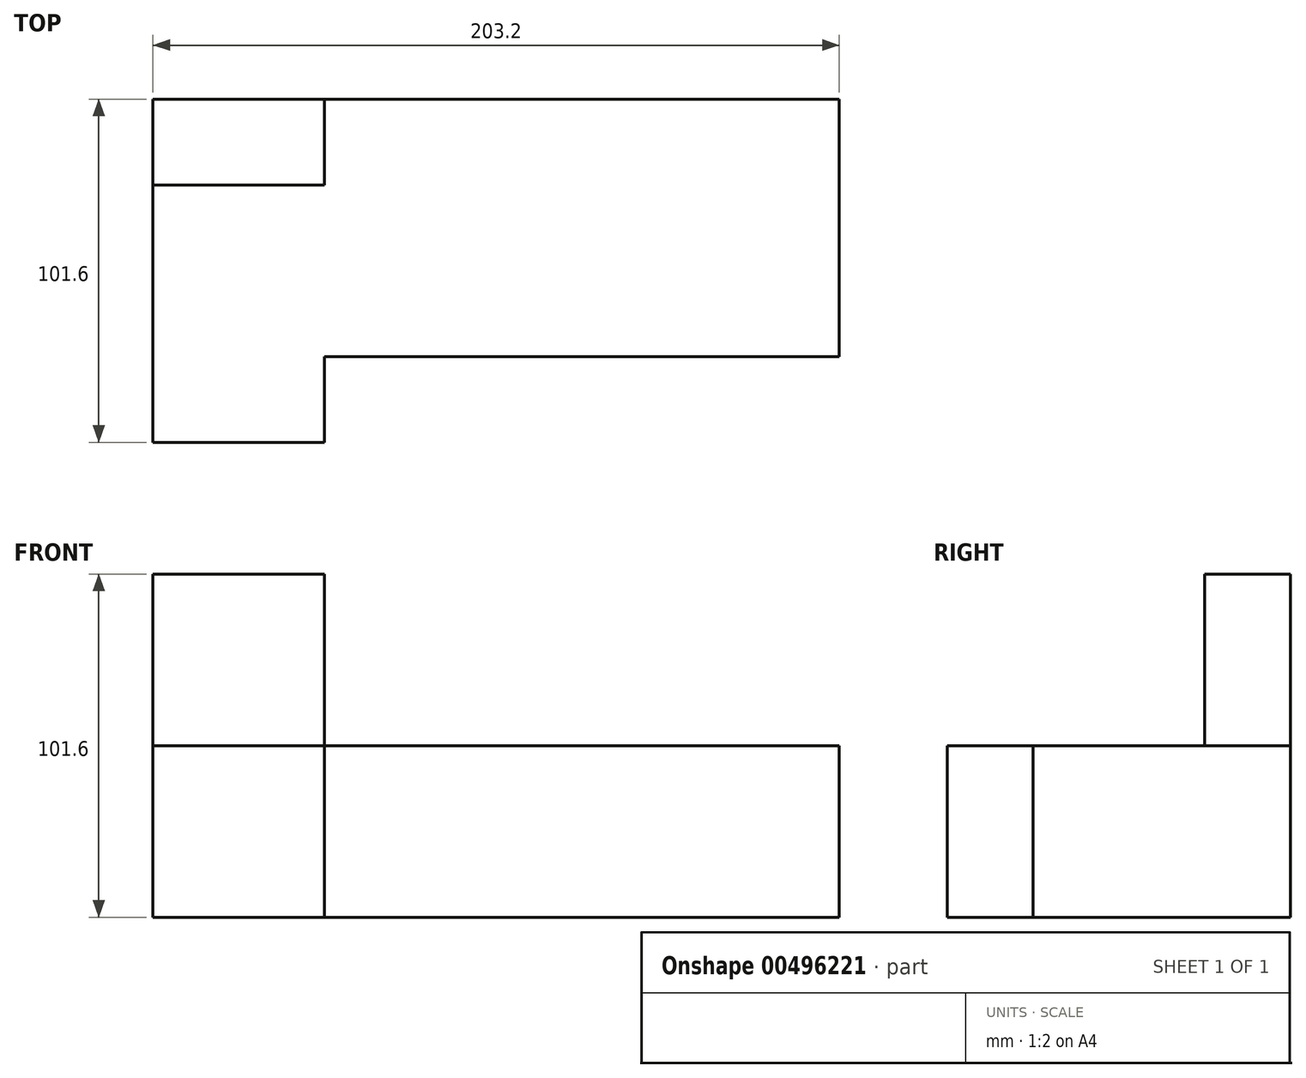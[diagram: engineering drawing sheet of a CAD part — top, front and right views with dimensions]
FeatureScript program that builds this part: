
annotation { "Feature Type Name" : "Feature", "Feature Type Description" : "" }
export const myFeature = defineFeature(function(context is Context, id is Id, definition is map)
    precondition{}
    {
        {
            var Q0;
            Q0=qCreatedBy(makeId("Top.planeOp"),FACE);
            var sketch = newSketch(context, id + "F0", { "sketchPlane" : qUnion([Q0])});
            skLineSegment(sketch, "E0.bottom", {"start": v(-75.87, 0) * mm, "end": v(127.33, 0) * mm});
            skLineSegment(sketch, "E0.top", {"start": v(-75.87, -101.6) * mm, "end": v(-25.07, -101.6) * mm});
            skLineSegment(sketch, "E0.left", {"start": v(-75.87, 0) * mm, "end": v(-75.87, -101.6) * mm});
            skLineSegment(sketch, "E0.right", {"start": v(127.33, 0) * mm, "end": v(127.33, -76.2) * mm});
            skLineSegment(sketch, "E1.top", {"start": v(-25.07, -76.2) * mm, "end": v(127.33, -76.2) * mm});
            skLineSegment(sketch, "E1.left", {"start": v(-25.07, -101.6) * mm, "end": v(-25.07, -76.2) * mm});
            skSolve(sketch);
        }
        {
            var Q0;
            Q0 = qSketchRegion(id + "F0", true);
            extrude(context, id + "F1", {"entities" : qUnion([Q0]), "depth" : 50.8 * mm});
        }
        {
            var Q0;
            Q0=makeQuery(id+"F1.opExtrude","CAP_FACE",FACE,{"disambiguationData":[OSD([sQuery(id+"F0.wireOp",EDGE,"E0.bottom"),sQuery(id+"F0.wireOp",EDGE,"E0.top"),sQuery(id+"F0.wireOp",EDGE,"E0.left"),sQuery(id+"F0.wireOp",EDGE,"E0.right"),sQuery(id+"F0.wireOp",EDGE,"E1.top"),sQuery(id+"F0.wireOp",EDGE,"E1.left")])],"isStart":false});
            var sketch = newSketch(context, id + "F2", { "sketchPlane" : qUnion([Q0])});
            skLineSegment(sketch, "E2.bottom", {"start": v(-75.87, 0) * mm, "end": v(-25.07, 0) * mm});
            skLineSegment(sketch, "E2.top", {"start": v(-75.87, -25.4) * mm, "end": v(-25.07, -25.4) * mm});
            skLineSegment(sketch, "E2.left", {"start": v(-75.87, 0) * mm, "end": v(-75.87, -25.4) * mm});
            skLineSegment(sketch, "E2.right", {"start": v(-25.07, 0) * mm, "end": v(-25.07, -25.4) * mm});
            skSolve(sketch);
        }
        {
            var Q0;
            Q0 = qSketchRegion(id + "F2", true);
            extrude(context, id + "F3", {"entities" : qUnion([Q0]), "operationType" : NewBodyOperationType.ADD, "depth" : 50.8 * mm});
        }
    });
